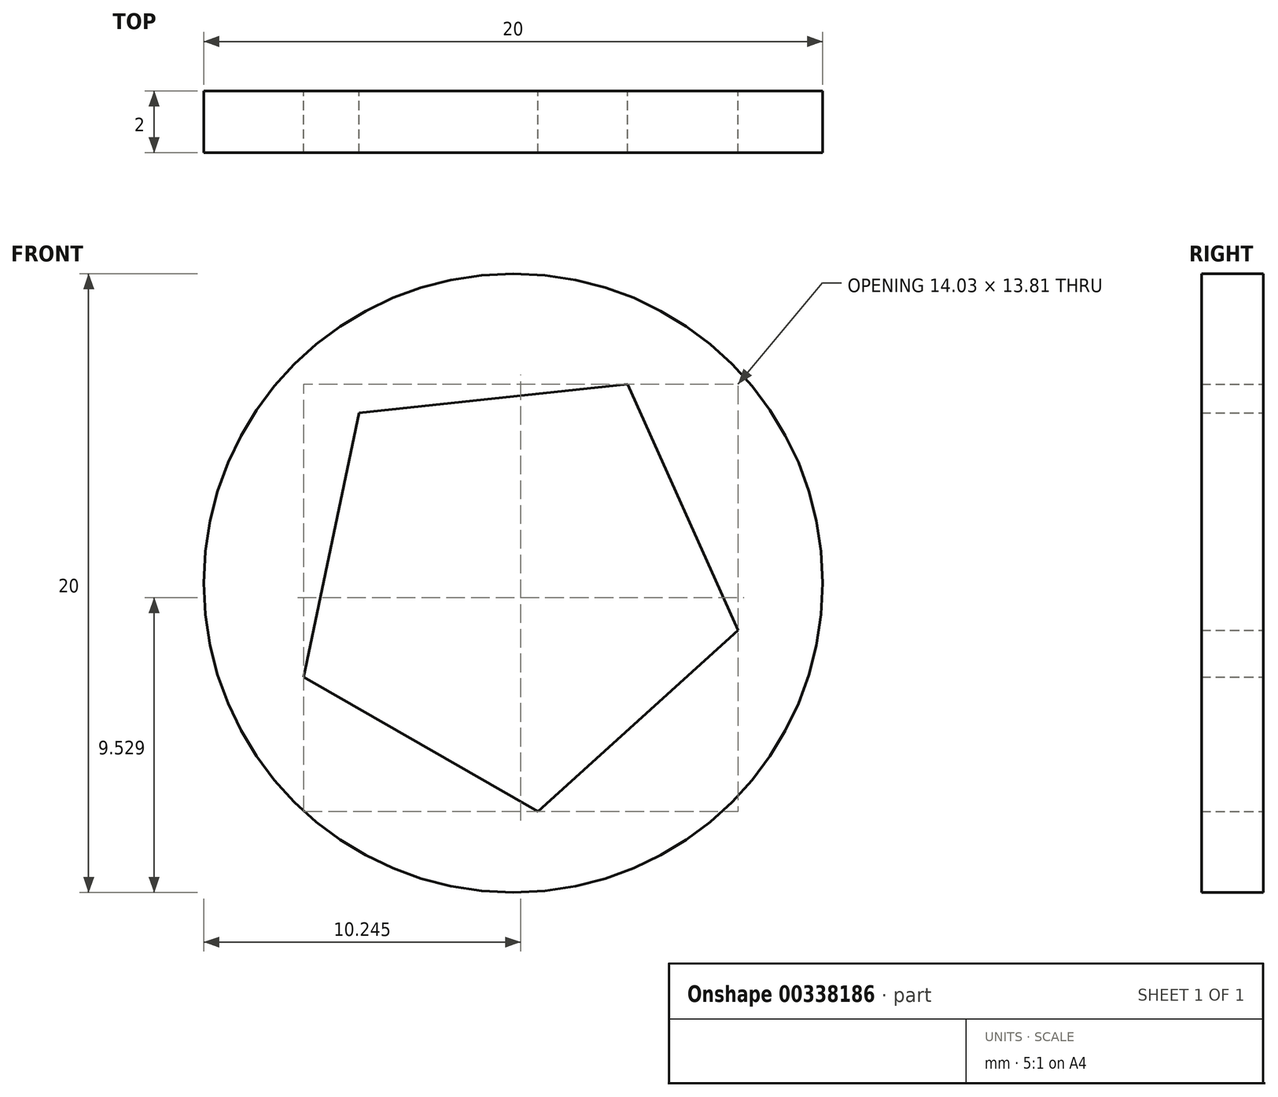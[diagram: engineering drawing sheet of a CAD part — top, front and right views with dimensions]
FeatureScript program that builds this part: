
annotation { "Feature Type Name" : "Feature", "Feature Type Description" : "" }
export const myFeature = defineFeature(function(context is Context, id is Id, definition is map)
    precondition{}
    {
        {
            var Q0;
            Q0=qCreatedBy(makeId("Front.planeOp"),FACE);
            var sketch = newSketch(context, id + "F0", { "sketchPlane" : qUnion([Q0])});
            skCircle(sketch, "E0", {"center": v(0, 0) * mm, "radius": 10 * mm});
            skCircle(sketch, "E1.cCircle", {"center": v(0, 0) * mm, "radius": 6 * mm, "construction": true});
            skLineSegment(sketch, "E1.0", {"start": v(7.26, -1.52) * mm, "end": v(0.8, -7.37) * mm});
            skLineSegment(sketch, "E1.1", {"start": v(0.8, -7.37) * mm, "end": v(-6.77, -3.03) * mm});
            skLineSegment(sketch, "E1.2", {"start": v(-6.77, -3.03) * mm, "end": v(-4.98, 5.5) * mm});
            skLineSegment(sketch, "E1.3", {"start": v(-4.98, 5.5) * mm, "end": v(3.7, 6.43) * mm});
            skLineSegment(sketch, "E1.4", {"start": v(3.7, 6.43) * mm, "end": v(7.26, -1.52) * mm});
            skPoint(sketch, "E1.0.midPoint", {"position": v(4.03, -4.45) * mm});
            skSolve(sketch);
        }
        {
            var Q0;
            Q0=makeQuery(id+"F0.imprint","IMPRINT",FACE,{"disambiguationData":[TD([[makeQuery(id+"F0.imprint","IMPRINT",EDGE,{"derivedFrom":sQuery(id+"F0.wireOp",EDGE,"E0")}),1.0]])]});
            extrude(context, id + "F1", {"entities" : qUnion([Q0]), "depth" : 2 * mm});
        }
    });
